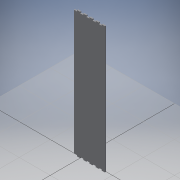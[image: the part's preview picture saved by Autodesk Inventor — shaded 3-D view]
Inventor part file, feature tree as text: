
AUTODESK INVENTOR PART (.ipt)
format: ipt  version: 2019 (Build 230136000, 136)  size: 139,776 bytes
history: native  units: mm
features: reference x21, other x5, extrude x1, sketch x1
ambient origin geometry x8: Origin, YZ Plane, XZ Plane, XY Plane, X Axis, Y Axis, Z Axis, Center Point
bodies: Body1 (feature_tree)
feature tree (28):
  other  "Твердое тело1"
  extrude  "Выдавливание1"  Depth=4.0mm TaperAngle=0.0deg
  sketch  "Эскиз1"
  reference  "Ссылка1"
  reference  "Ссылка2"
  reference  "Ссылка3"
  reference  "Ссылка4"
  reference  "Ссылка5"
  reference  "Ссылка6"
  reference  "Ссылка7"
  reference  "Ссылка8"
  reference  "Ссылка9"
  reference  "Ссылка10"
  reference  "Ссылка11"
  reference  "Ссылка12"
  reference  "Ссылка13"
  reference  "Ссылка14"
  reference  "Ссылка15"
  reference  "Ссылка16"
  reference  "Ссылка17"
  reference  "Ссылка18"
  reference  "Ссылка19"
  reference  "Ссылка20"
  reference  "Ссылка21"
  parser-record x1  (decoder bookkeeping rows leaked as tree rows — omitted from the tree; the rows remain in map.json)
  other  "kowsh.iam"
  other  "боковушка:2"
  other  "боковушка:1"
note: 1 file-system path scrubbed to <path> (originals preserved in map.json)
